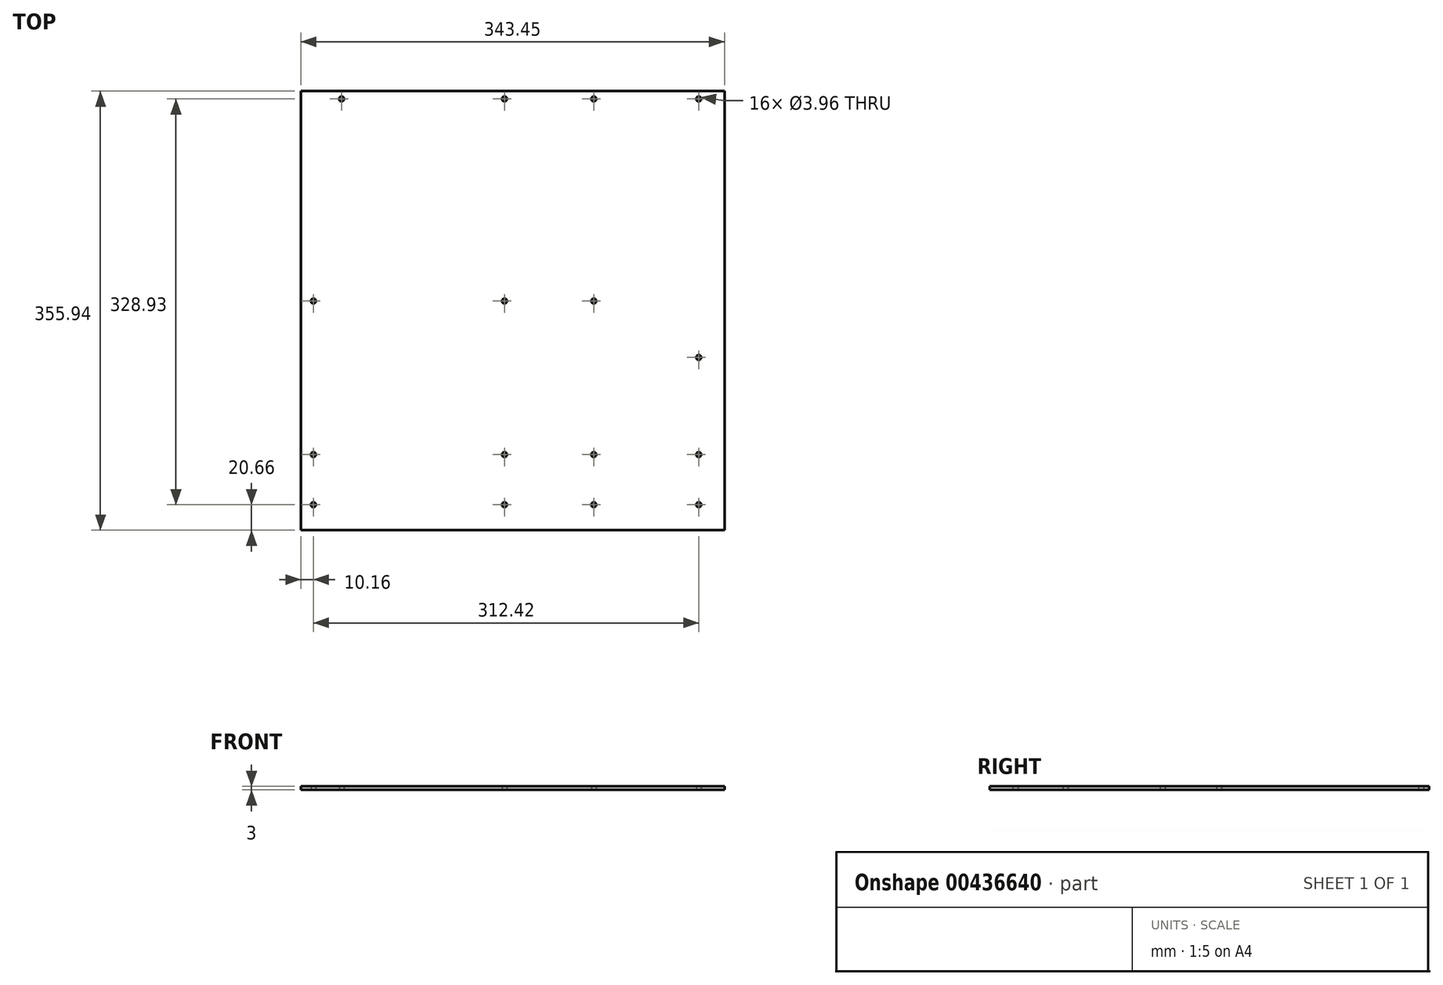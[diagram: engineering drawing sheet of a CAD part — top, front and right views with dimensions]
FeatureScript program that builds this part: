
annotation { "Feature Type Name" : "Feature", "Feature Type Description" : "" }
export const myFeature = defineFeature(function(context is Context, id is Id, definition is map)
    precondition{}
    {
        {
            var Q0;
            Q0=qCreatedBy(makeId("Top.planeOp"),FACE);
            var sketch = newSketch(context, id + "F0", { "sketchPlane" : qUnion([Q0])});
            skLineSegment(sketch, "E0", {"start": v(0, 0) * mm, "end": v(33.02, 0) * mm, "construction": true});
            skCircle(sketch, "E1", {"center": v(33.02, 0) * mm, "radius": 1.98 * mm});
            skLineSegment(sketch, "E2", {"start": v(33.02, 0) * mm, "end": v(165.1, 0) * mm, "construction": true});
            skCircle(sketch, "E3", {"center": v(165.1, 0) * mm, "radius": 1.98 * mm});
            skLineSegment(sketch, "E4", {"start": v(165.1, 0) * mm, "end": v(237.5, 0) * mm, "construction": true});
            skCircle(sketch, "E5", {"center": v(237.5, 0) * mm, "radius": 1.98 * mm});
            skLineSegment(sketch, "E6", {"start": v(0, -163.83) * mm, "end": v(0, 0) * mm, "construction": true});
            skLineSegment(sketch, "E7", {"start": v(0, -163.83) * mm, "end": v(10.16, -163.83) * mm, "construction": true});
            skCircle(sketch, "E8", {"center": v(10.16, -163.83) * mm, "radius": 1.98 * mm});
            skLineSegment(sketch, "E9", {"start": v(165.1, -163.83) * mm, "end": v(10.16, -163.83) * mm, "construction": true});
            skLineSegment(sketch, "E10", {"start": v(165.1, -163.83) * mm, "end": v(237.5, -163.83) * mm, "construction": true});
            skLineSegment(sketch, "E11", {"start": v(0, -163.83) * mm, "end": v(0, -288.3) * mm, "construction": true});
            skLineSegment(sketch, "E12", {"start": v(0, -288.3) * mm, "end": v(10.16, -288.3) * mm, "construction": true});
            skLineSegment(sketch, "E13", {"start": v(10.16, -288.3) * mm, "end": v(165.1, -288.3) * mm, "construction": true});
            skLineSegment(sketch, "E14", {"start": v(165.1, -288.3) * mm, "end": v(237.5, -288.3) * mm, "construction": true});
            skCircle(sketch, "E15", {"center": v(165.1, -163.83) * mm, "radius": 1.98 * mm});
            skCircle(sketch, "E16", {"center": v(237.5, -163.83) * mm, "radius": 1.98 * mm});
            skCircle(sketch, "E17", {"center": v(10.16, -288.3) * mm, "radius": 1.98 * mm});
            skCircle(sketch, "E18", {"center": v(165.1, -288.3) * mm, "radius": 1.98 * mm});
            skCircle(sketch, "E19", {"center": v(237.5, -288.3) * mm, "radius": 1.98 * mm});
            skLineSegment(sketch, "E20", {"start": v(0, 0) * mm, "end": v(0, 6.35) * mm, "construction": true});
            skLineSegment(sketch, "E21", {"start": v(0, -288.3) * mm, "end": v(0, -328.93) * mm, "construction": true});
            skLineSegment(sketch, "E22", {"start": v(0, -328.93) * mm, "end": v(10.16, -328.93) * mm, "construction": true});
            skLineSegment(sketch, "E23", {"start": v(10.16, -328.93) * mm, "end": v(165.1, -328.93) * mm, "construction": true});
            skLineSegment(sketch, "E24", {"start": v(165.1, -328.93) * mm, "end": v(237.5, -328.93) * mm, "construction": true});
            skCircle(sketch, "E25", {"center": v(10.16, -328.93) * mm, "radius": 1.98 * mm});
            skCircle(sketch, "E26", {"center": v(165.1, -328.93) * mm, "radius": 1.98 * mm});
            skCircle(sketch, "E27", {"center": v(237.5, -328.93) * mm, "radius": 1.98 * mm});
            skLineSegment(sketch, "E28", {"start": v(237.5, 0) * mm, "end": v(322.58, 0) * mm, "construction": true});
            skLineSegment(sketch, "E29", {"start": v(322.58, -288.3) * mm, "end": v(237.5, -288.3) * mm, "construction": true});
            skLineSegment(sketch, "E30", {"start": v(237.5, -328.93) * mm, "end": v(322.58, -328.93) * mm, "construction": true});
            skLineSegment(sketch, "E31", {"start": v(322.58, 0) * mm, "end": v(322.58, -209.55) * mm, "construction": true});
            skCircle(sketch, "E32", {"center": v(322.58, 0) * mm, "radius": 1.98 * mm});
            skCircle(sketch, "E33", {"center": v(322.58, -209.55) * mm, "radius": 1.98 * mm});
            skCircle(sketch, "E34", {"center": v(322.58, -288.3) * mm, "radius": 1.98 * mm});
            skCircle(sketch, "E35", {"center": v(322.58, -328.93) * mm, "radius": 1.98 * mm});
            skLineSegment(sketch, "E36.bottom", {"start": v(0, 6.35) * mm, "end": v(343.45, 6.35) * mm});
            skLineSegment(sketch, "E36.top", {"start": v(0, -349.59) * mm, "end": v(343.45, -349.59) * mm});
            skLineSegment(sketch, "E36.left", {"start": v(0, 6.35) * mm, "end": v(0, -349.59) * mm});
            skLineSegment(sketch, "E36.right", {"start": v(343.45, 6.35) * mm, "end": v(343.45, -349.59) * mm});
            skSolve(sketch);
        }
        {
            var Q0;
            Q0=makeQuery(id+"F0.imprint","IMPRINT",FACE,{"disambiguationData":[TD([[makeQuery(id+"F0.imprint","IMPRINT",EDGE,{"derivedFrom":sQuery(id+"F0.wireOp",EDGE,"E1")}),-1.0]])]});
            extrude(context, id + "F1", {"entities" : qUnion([Q0]), "depth" : 3 * mm});
        }
    });
